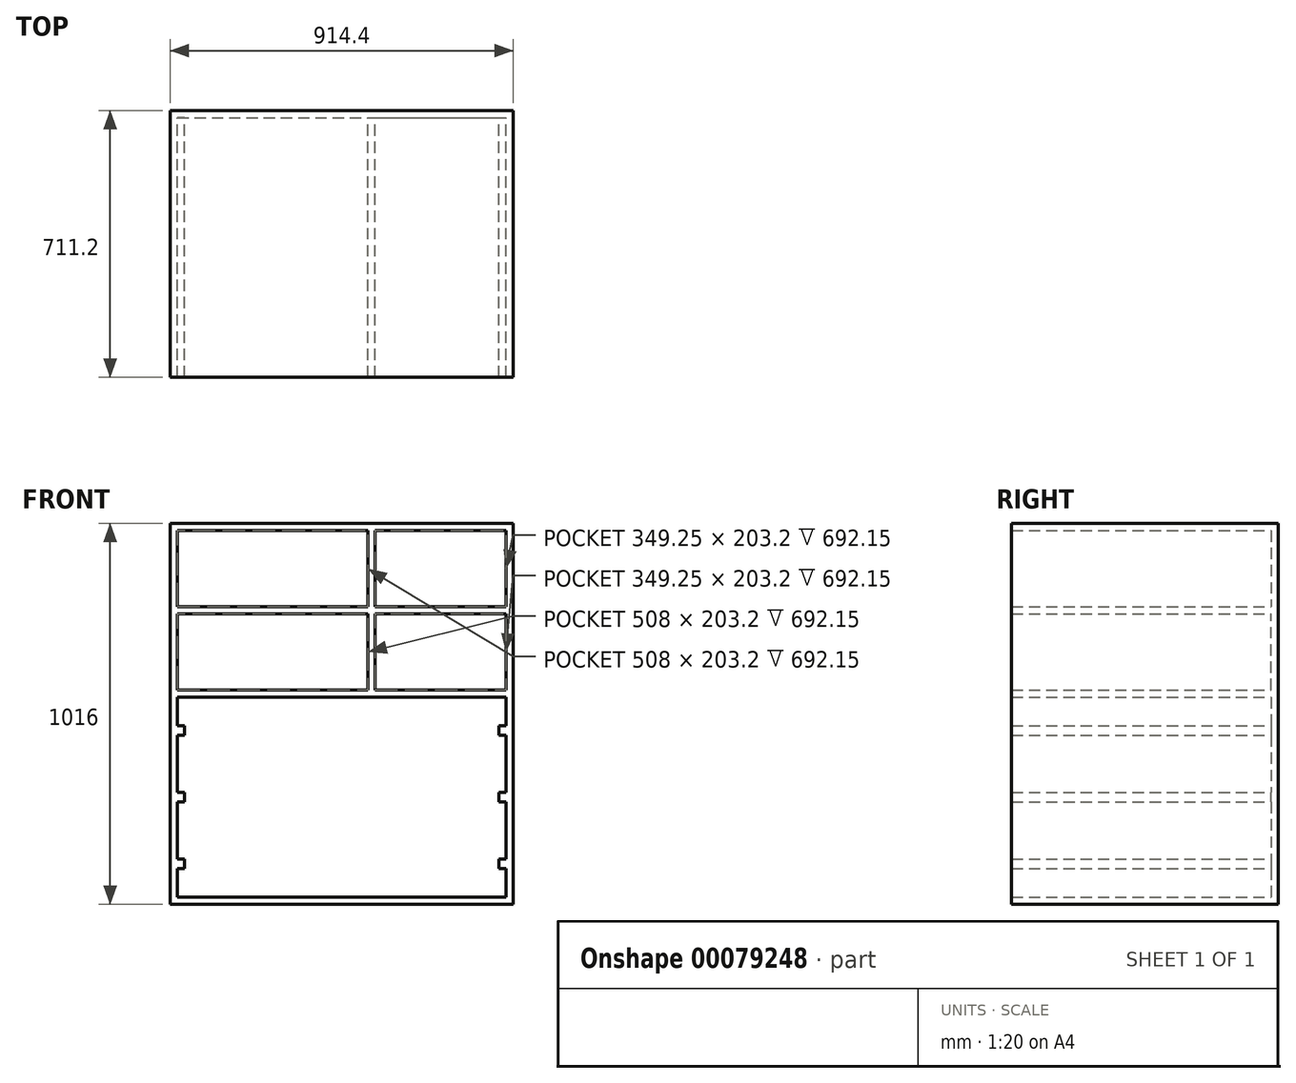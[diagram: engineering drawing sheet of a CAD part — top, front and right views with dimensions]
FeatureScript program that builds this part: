
annotation { "Feature Type Name" : "Feature", "Feature Type Description" : "" }
export const myFeature = defineFeature(function(context is Context, id is Id, definition is map)
    precondition{}
    {
        {
            var Q0;
            Q0=qCreatedBy(makeId("Front.planeOp"),FACE);
            var sketch = newSketch(context, id + "F0", { "sketchPlane" : qUnion([Q0])});
            skLineSegment(sketch, "E0.bottom", {"start": v(457.2, 508) * mm, "end": v(-457.2, 508) * mm});
            skLineSegment(sketch, "E0.top", {"start": v(457.2, -508) * mm, "end": v(-457.2, -508) * mm});
            skLineSegment(sketch, "E0.left", {"start": v(457.2, 508) * mm, "end": v(457.2, -508) * mm});
            skLineSegment(sketch, "E0.right", {"start": v(-457.2, 508) * mm, "end": v(-457.2, -508) * mm});
            skPoint(sketch, "E0.middle", {"position": v(0, 0) * mm});
            skLineSegment(sketch, "E1.top", {"start": v(438.15, 285.75) * mm, "end": v(88.9, 285.75) * mm});
            skLineSegment(sketch, "E1.left", {"start": v(69.85, 488.95) * mm, "end": v(69.85, 285.75) * mm});
            skLineSegment(sketch, "E1.right", {"start": v(-438.15, 488.95) * mm, "end": v(-438.15, 285.75) * mm});
            skPoint(sketch, "E1.middle", {"position": v(-184.15, 387.35) * mm});
            skLineSegment(sketch, "E2.bottom", {"start": v(88.9, 488.95) * mm, "end": v(438.15, 488.95) * mm});
            skLineSegment(sketch, "E2.left", {"start": v(88.9, 488.95) * mm, "end": v(88.9, 285.75) * mm});
            skLineSegment(sketch, "E2.right", {"start": v(438.15, 488.95) * mm, "end": v(438.15, 285.75) * mm});
            skPoint(sketch, "E2.middle", {"position": v(263.53, 412.75) * mm});
            skLineSegment(sketch, "E3", {"start": v(-438.15, 488.95) * mm, "end": v(69.85, 488.95) * mm});
            skLineSegment(sketch, "E4", {"start": v(-438.15, 266.7) * mm, "end": v(69.85, 266.7) * mm});
            skLineSegment(sketch, "E5", {"start": v(88.9, 285.75) * mm, "end": v(88.9, 317.5) * mm});
            skLineSegment(sketch, "E6", {"start": v(438.15, 63.5) * mm, "end": v(88.9, 63.5) * mm});
            skLineSegment(sketch, "E7", {"start": v(-438.15, 63.5) * mm, "end": v(-438.15, 266.7) * mm});
            skLineSegment(sketch, "E8.bottom", {"start": v(-438.15, 44.45) * mm, "end": v(438.15, 44.45) * mm});
            skLineSegment(sketch, "E8.top", {"start": v(-438.15, -488.95) * mm, "end": v(438.15, -488.95) * mm});
            skLineSegment(sketch, "E8.left", {"start": v(-438.15, 44.45) * mm, "end": v(-438.15, -488.95) * mm});
            skLineSegment(sketch, "E8.right", {"start": v(438.15, 44.45) * mm, "end": v(438.15, -488.95) * mm});
            skLineSegment(sketch, "E9.bottom", {"start": v(-419.04, -31.75) * mm, "end": v(-438.15, -31.75) * mm});
            skLineSegment(sketch, "E9.top", {"start": v(-419.04, -57.15) * mm, "end": v(-438.15, -57.15) * mm});
            skLineSegment(sketch, "E9.left", {"start": v(-419.04, -31.75) * mm, "end": v(-419.04, -57.15) * mm});
            skLineSegment(sketch, "E10.MirrorCS", {"start": v(419.04, -31.75) * mm, "end": v(438.15, -31.75) * mm});
            skLineSegment(sketch, "E11.MirrorCS", {"start": v(419.04, -31.75) * mm, "end": v(419.04, -57.15) * mm});
            skLineSegment(sketch, "E12.MirrorCS", {"start": v(419.04, -57.15) * mm, "end": v(438.15, -57.15) * mm});
            skLineSegment(sketch, "E13.MirrorCS", {"start": v(-419.04, -234.95) * mm, "end": v(-419.04, -209.55) * mm});
            skLineSegment(sketch, "E14.MirrorCS", {"start": v(-419.04, -234.95) * mm, "end": v(-438.15, -234.95) * mm});
            skLineSegment(sketch, "E15.MirrorCS", {"start": v(-419.04, -209.55) * mm, "end": v(-438.15, -209.55) * mm});
            skLineSegment(sketch, "E16.MirrorCS", {"start": v(419.04, -209.55) * mm, "end": v(438.15, -209.55) * mm});
            skLineSegment(sketch, "E17.MirrorCS", {"start": v(419.04, -234.95) * mm, "end": v(419.04, -209.55) * mm});
            skLineSegment(sketch, "E18.MirrorCS", {"start": v(419.04, -234.95) * mm, "end": v(438.15, -234.95) * mm});
            skLineSegment(sketch, "E19.MirrorCS", {"start": v(-419.04, -387.35) * mm, "end": v(-419.04, -412.75) * mm});
            skLineSegment(sketch, "E20.MirrorCS", {"start": v(-419.04, -412.75) * mm, "end": v(-438.15, -412.75) * mm});
            skLineSegment(sketch, "E21.MirrorCS", {"start": v(-419.04, -387.35) * mm, "end": v(-438.15, -387.35) * mm});
            skLineSegment(sketch, "E22.MirrorCS", {"start": v(419.04, -412.75) * mm, "end": v(438.15, -412.75) * mm});
            skLineSegment(sketch, "E23.MirrorCS", {"start": v(419.04, -387.35) * mm, "end": v(419.04, -412.75) * mm});
            skLineSegment(sketch, "E24.MirrorCS", {"start": v(419.04, -387.35) * mm, "end": v(438.15, -387.35) * mm});
            skPoint(sketch, "E25.orphan", {"position": v(69.85, 285.75) * mm});
            skLineSegment(sketch, "E26.trimOffspring", {"start": v(88.9, 266.7) * mm, "end": v(438.15, 266.7) * mm});
            skLineSegment(sketch, "E27.trimOffspring", {"start": v(69.85, 285.75) * mm, "end": v(-438.15, 285.75) * mm});
            skLineSegment(sketch, "E28.trimOffspring", {"start": v(69.85, 266.7) * mm, "end": v(69.85, 63.5) * mm});
            skLineSegment(sketch, "E29.trimOffspring", {"start": v(69.85, 63.5) * mm, "end": v(-438.15, 63.5) * mm});
            skLineSegment(sketch, "E30.trimOffspring", {"start": v(88.9, 266.7) * mm, "end": v(88.9, 63.5) * mm});
            skPoint(sketch, "E31.orphan", {"position": v(438.15, 336.55) * mm});
            skLineSegment(sketch, "E32.trimOffspring", {"start": v(438.15, 266.7) * mm, "end": v(438.15, 63.5) * mm});
            skSolve(sketch);
        }
        {
            var Q0;
            Q0=makeQuery(id+"F0.imprint","IMPRINT",FACE,{"disambiguationData":[TD([[makeQuery(id+"F0.imprint","IMPRINT",EDGE,{"derivedFrom":sQuery(id+"F0.wireOp",EDGE,"E0.bottom")}),1.0]])]});
            var Q1;
            Q1=makeQuery(id+"F0.imprint","IMPRINT",FACE,{"disambiguationData":[TD([[makeQuery(id+"F0.imprint","IMPRINT",EDGE,{"derivedFrom":sQuery(id+"F0.wireOp",EDGE,"E1.top")}),-1.0]])]});
            var Q2;
            Q2=makeQuery(id+"F0.imprint","IMPRINT",FACE,{"disambiguationData":[TD([[makeQuery(id+"F0.imprint","IMPRINT",EDGE,{"derivedFrom":sQuery(id+"F0.wireOp",EDGE,"E2.bottom")}),-1.0]])]});
            var Q3;
            Q3=makeQuery(id+"F0.imprint","IMPRINT",FACE,{"disambiguationData":[TD([[makeQuery(id+"F0.imprint","IMPRINT",EDGE,{"derivedFrom":sQuery(id+"F0.wireOp",EDGE,"E4")}),-1.0]])]});
            var Q4;
            Q4=makeQuery(id+"F0.imprint","IMPRINT",FACE,{"disambiguationData":[TD([[makeQuery(id+"F0.imprint","IMPRINT",EDGE,{"derivedFrom":sQuery(id+"F0.wireOp",EDGE,"E8.bottom")}),-1.0]])]});
            var Q5;
            {var subQ0=sQuery(id+"F0.wireOp",EDGE,"E9.bottom");Q5=makeQuery(id+"F0.imprint","IMPRINT",FACE,{"disambiguationData":[TD([[makeQuery(id+"F0.imprint","IMPRINT",EDGE,{"derivedFrom":subQ0}),1.0]])]});}
            var Q6;
            Q6=makeQuery(id+"F0.imprint","IMPRINT",FACE,{"disambiguationData":[TD([[makeQuery(id+"F0.imprint","IMPRINT",EDGE,{"derivedFrom":sQuery(id+"F0.wireOp",EDGE,"E13.MirrorCS")}),1.0]])]});
            var Q7;
            Q7=makeQuery(id+"F0.imprint","IMPRINT",FACE,{"disambiguationData":[TD([[makeQuery(id+"F0.imprint","IMPRINT",EDGE,{"derivedFrom":sQuery(id+"F0.wireOp",EDGE,"E19.MirrorCS")}),-1.0]])]});
            var Q8;
            {var subQ0=sQuery(id+"F0.wireOp",EDGE,"E22.MirrorCS");Q8=makeQuery(id+"F0.imprint","IMPRINT",FACE,{"disambiguationData":[TD([[makeQuery(id+"F0.imprint","IMPRINT",EDGE,{"derivedFrom":subQ0}),1.0]])]});}
            var Q9;
            {var subQ0=sQuery(id+"F0.wireOp",EDGE,"E16.MirrorCS");Q9=makeQuery(id+"F0.imprint","IMPRINT",FACE,{"disambiguationData":[TD([[makeQuery(id+"F0.imprint","IMPRINT",EDGE,{"derivedFrom":subQ0}),-1.0]])]});}
            var Q10;
            {var subQ0=sQuery(id+"F0.wireOp",EDGE,"E10.MirrorCS");Q10=makeQuery(id+"F0.imprint","IMPRINT",FACE,{"disambiguationData":[TD([[makeQuery(id+"F0.imprint","IMPRINT",EDGE,{"derivedFrom":subQ0}),-1.0]])]});}
            var Q11;
            Q11=makeQuery(id+"F0.imprint","IMPRINT",FACE,{"disambiguationData":[TD([[makeQuery(id+"F0.imprint","IMPRINT",EDGE,{"derivedFrom":sQuery(id+"F0.wireOp",EDGE,"E1.left")}),-1.0]])]});
            var Q12;
            Q12=makeQuery(id+"F0.imprint","IMPRINT",FACE,{"disambiguationData":[TD([[makeQuery(id+"F0.imprint","IMPRINT",EDGE,{"derivedFrom":sQuery(id+"F0.wireOp",EDGE,"E6")}),-1.0]])]});
            extrude(context, id + "F1", {"entities" : qUnion([Q0, Q1, Q2, Q3, Q4, Q5, Q6, Q7, Q8, Q9, Q10, Q11, Q12]), "oppositeDirection" : true, "depth" : 19.05 * mm});
        }
        {
            var Q0;
            Q0=makeQuery(id+"F0.imprint","IMPRINT",FACE,{"disambiguationData":[TD([[makeQuery(id+"F0.imprint","IMPRINT",EDGE,{"derivedFrom":sQuery(id+"F0.wireOp",EDGE,"E0.bottom")}),1.0]])]});
            var Q1;
            Q1=makeQuery(id+"F0.imprint","IMPRINT",FACE,{"disambiguationData":[TD([[makeQuery(id+"F0.imprint","IMPRINT",EDGE,{"derivedFrom":sQuery(id+"F0.wireOp",EDGE,"E19.MirrorCS")}),-1.0]])]});
            var Q2;
            Q2=makeQuery(id+"F0.imprint","IMPRINT",FACE,{"disambiguationData":[TD([[makeQuery(id+"F0.imprint","IMPRINT",EDGE,{"derivedFrom":sQuery(id+"F0.wireOp",EDGE,"E13.MirrorCS")}),1.0]])]});
            var Q3;
            {var subQ0=sQuery(id+"F0.wireOp",EDGE,"E9.bottom");Q3=makeQuery(id+"F0.imprint","IMPRINT",FACE,{"disambiguationData":[TD([[makeQuery(id+"F0.imprint","IMPRINT",EDGE,{"derivedFrom":subQ0}),1.0]])]});}
            var Q4;
            {var subQ0=sQuery(id+"F0.wireOp",EDGE,"E10.MirrorCS");Q4=makeQuery(id+"F0.imprint","IMPRINT",FACE,{"disambiguationData":[TD([[makeQuery(id+"F0.imprint","IMPRINT",EDGE,{"derivedFrom":subQ0}),-1.0]])]});}
            var Q5;
            {var subQ0=sQuery(id+"F0.wireOp",EDGE,"E16.MirrorCS");Q5=makeQuery(id+"F0.imprint","IMPRINT",FACE,{"disambiguationData":[TD([[makeQuery(id+"F0.imprint","IMPRINT",EDGE,{"derivedFrom":subQ0}),-1.0]])]});}
            var Q6;
            {var subQ0=sQuery(id+"F0.wireOp",EDGE,"E22.MirrorCS");Q6=makeQuery(id+"F0.imprint","IMPRINT",FACE,{"disambiguationData":[TD([[makeQuery(id+"F0.imprint","IMPRINT",EDGE,{"derivedFrom":subQ0}),1.0]])]});}
            extrude(context, id + "F2", {"entities" : qUnion([Q0, Q1, Q2, Q3, Q4, Q5, Q6]), "operationType" : NewBodyOperationType.ADD, "depth" : 692.15 * mm});
        }
    });
